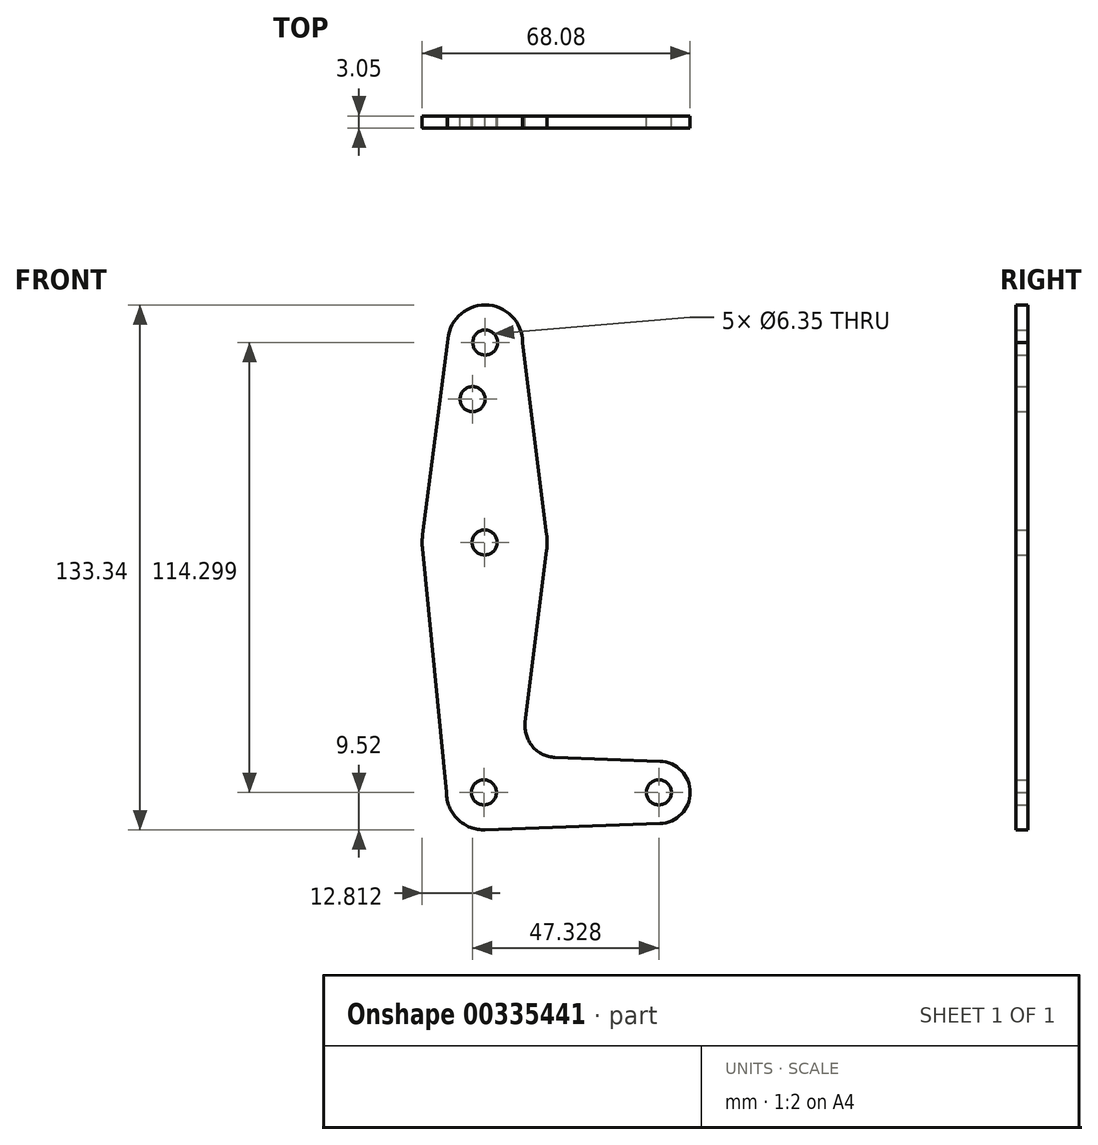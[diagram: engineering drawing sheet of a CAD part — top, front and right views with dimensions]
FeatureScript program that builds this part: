
annotation { "Feature Type Name" : "Feature", "Feature Type Description" : "" }
export const myFeature = defineFeature(function(context is Context, id is Id, definition is map)
    precondition{}
    {
        {
            var Q0;
            Q0=qCreatedBy(makeId("Front.planeOp"),FACE);
            var sketch = newSketch(context, id + "F0", { "sketchPlane" : qUnion([Q0])});
            skLineSegment(sketch, "E0", {"start": v(0, 0) * mm, "end": v(44.45, 0) * mm, "construction": true});
            skCircle(sketch, "E1", {"center": v(0, 0) * mm, "radius": 9.53 * mm});
            skCircle(sketch, "E2", {"center": v(0.34, 114.3) * mm, "radius": 9.53 * mm});
            skCircle(sketch, "E3", {"center": v(44.45, 0) * mm, "radius": 7.94 * mm});
            skLineSegment(sketch, "E4", {"start": v(0.34, 114.3) * mm, "end": v(0, 0) * mm, "construction": true});
            skLineSegment(sketch, "E5", {"start": v(15.94, 61.54) * mm, "end": v(10.5, 17.8) * mm});
            skLineSegment(sketch, "E6", {"start": v(0.34, -9.52) * mm, "end": v(44.73, -7.93) * mm});
            skLineSegment(sketch, "E7", {"start": v(18.1, 8.88) * mm, "end": v(44.73, 7.93) * mm});
            skCircle(sketch, "E8", {"center": v(0.34, 114.3) * mm, "radius": 3.18 * mm});
            skCircle(sketch, "E9", {"center": v(0.19, 63.5) * mm, "radius": 3.18 * mm});
            skCircle(sketch, "E10", {"center": v(0, 0) * mm, "radius": 3.18 * mm});
            skCircle(sketch, "E11", {"center": v(44.45, 0) * mm, "radius": 3.18 * mm});
            skCircle(sketch, "E12", {"center": v(-2.88, 99.9) * mm, "radius": 3.18 * mm});
            skCircle(sketch, "E13", {"center": v(0.19, 63.5) * mm, "radius": 15.88 * mm});
            skLineSegment(sketch, "E14", {"start": v(-9.18, 114.3) * mm, "end": v(-15.55, 65.56) * mm});
            skLineSegment(sketch, "E15", {"start": v(9.87, 114.3) * mm, "end": v(15.94, 65.46) * mm});
            skLineSegment(sketch, "E16", {"start": v(-15.6, 61.95) * mm, "end": v(-9.53, 0) * mm});
            skArc(sketch, "E17.filletArc", {"start": v(10.5, 17.8) * mm, "mid": v(12.34, 11.67) * mm, "end": v(18.1, 8.88) * mm});
            skSolve(sketch);
        }
        {
            var Q0;
            Q0 = qSketchRegion(id + "F0", true);
            extrude(context, id + "F1", {"entities" : qUnion([Q0]), "depth" : 3.05 * mm});
        }
    });
